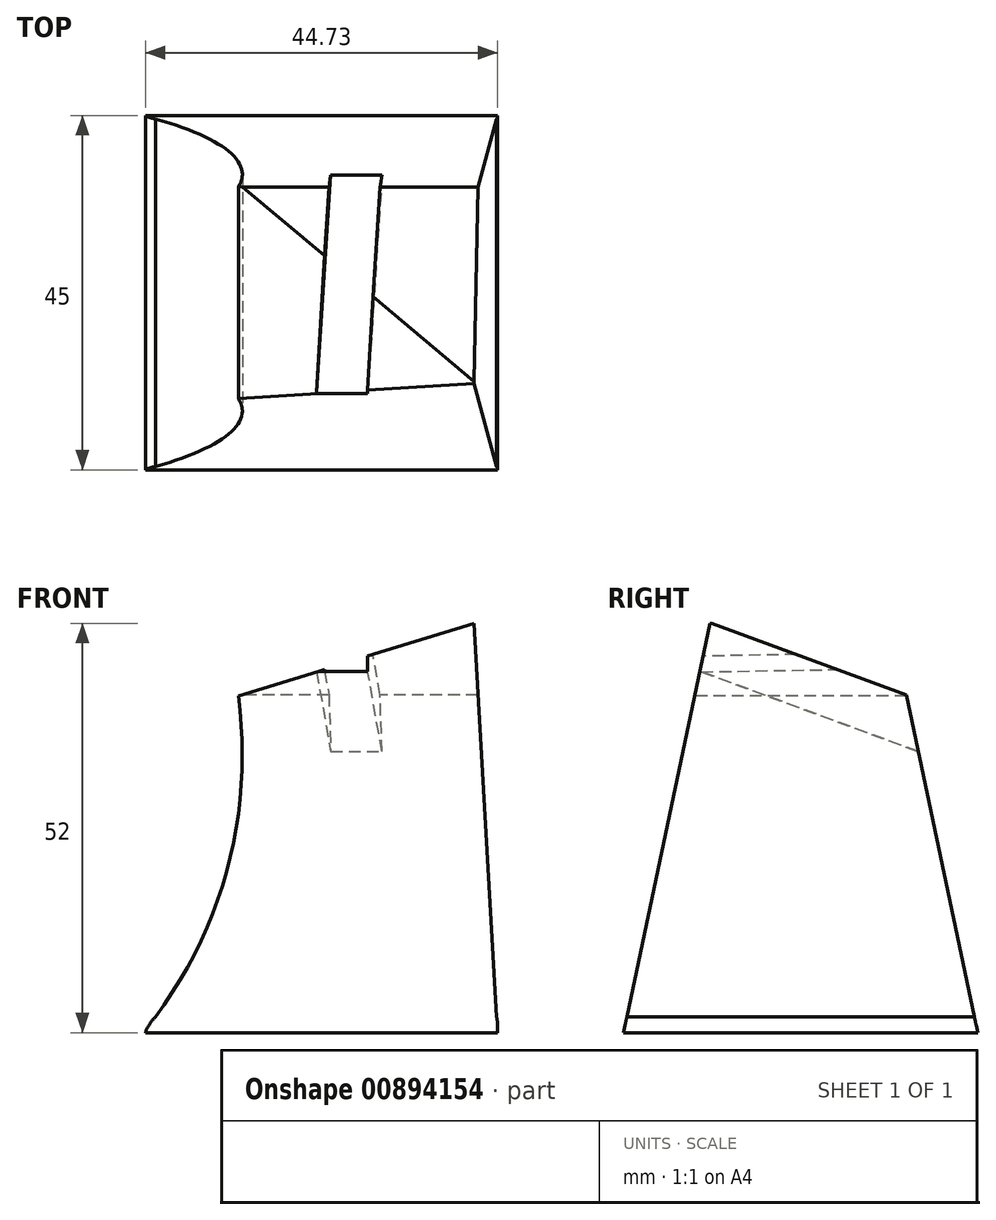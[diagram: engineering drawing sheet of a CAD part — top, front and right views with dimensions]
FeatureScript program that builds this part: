
annotation { "Feature Type Name" : "Feature", "Feature Type Description" : "" }
export const myFeature = defineFeature(function(context is Context, id is Id, definition is map)
    precondition{}
    {
        {
            var Q0;
            Q0=qCreatedBy(makeId("Top.planeOp"),FACE);
            var sketch = newSketch(context, id + "F0", { "sketchPlane" : qUnion([Q0])});
            skLineSegment(sketch, "E0", {"start": v(0, 45) * mm, "end": v(0, 0) * mm});
            skLineSegment(sketch, "E1.0", {"start": v(-45, 45) * mm, "end": v(-45, 0) * mm});
            skLineSegment(sketch, "E2", {"start": v(-45, 45) * mm, "end": v(0, 45) * mm});
            skLineSegment(sketch, "E3", {"start": v(-45, 0) * mm, "end": v(0, 0) * mm});
            skSolve(sketch);
        }
        {
            var Q0;
            Q0=makeQuery(id+"F0.imprint","IMPRINT",FACE,{"disambiguationData":[TD([[makeQuery(id+"F0.imprint","IMPRINT",EDGE,{"derivedFrom":sQuery(id+"F0.wireOp",EDGE,"E0")}),-1.0]])]});
            extrude(context, id + "F1", {"entities" : qUnion([Q0]), "depth" : 2 * mm, "offsetDistance" : 25 * mm});
        }
        {
            var Q0;
            Q0=qCreatedBy(makeId("Front.planeOp"),FACE);
            var sketch = newSketch(context, id + "F2", { "sketchPlane" : qUnion([Q0])});
            skLineSegment(sketch, "E4", {"start": v(0, 0) * mm, "end": v(-3, 52) * mm});
            skLineSegment(sketch, "E5", {"start": v(-3, 52) * mm, "end": v(-32.92, 42.77) * mm});
            skArc(sketch, "E6", {"start": v(-45, 0) * mm, "mid": v(-34.5, 20.13) * mm, "end": v(-32.92, 42.77) * mm});
            skLineSegment(sketch, "E7", {"start": v(-45, 0) * mm, "end": v(0, 0) * mm});
            skSolve(sketch);
        }
        {
            var Q0;
            Q0=makeQuery(id+"F2.imprint","IMPRINT",FACE,{"disambiguationData":[TD([[makeQuery(id+"F2.imprint","IMPRINT",EDGE,{"derivedFrom":sQuery(id+"F2.wireOp",EDGE,"E4")}),1.0]])]});
            extrude(context, id + "F3", {"entities" : qUnion([Q0]), "operationType" : NewBodyOperationType.ADD, "oppositeDirection" : true, "depth" : 45 * mm, "offsetDistance" : 25 * mm});
        }
        {
            var Q0;
            Q0=qCreatedBy(makeId("Right.planeOp"),FACE);
            var sketch = newSketch(context, id + "F4", { "sketchPlane" : qUnion([Q0])});
            skLineSegment(sketch, "E8", {"start": v(12.5, 59.13) * mm, "end": v(0, 0) * mm});
            skLineSegment(sketch, "E9", {"start": v(12.5, 59.13) * mm, "end": v(0, 59.13) * mm});
            skLineSegment(sketch, "E10", {"start": v(0, 59.13) * mm, "end": v(0, 0) * mm});
            skLineSegment(sketch, "E11.0", {"start": v(45, 59.13) * mm, "end": v(45, 0) * mm});
            skLineSegment(sketch, "E12", {"start": v(45, 0) * mm, "end": v(32.5, 59.13) * mm});
            skLineSegment(sketch, "E13", {"start": v(45, 59.13) * mm, "end": v(32.5, 59.13) * mm});
            skSolve(sketch);
        }
        {
            var Q0;
            Q0=makeQuery(id+"F4.imprint","IMPRINT",FACE,{"disambiguationData":[TD([[makeQuery(id+"F4.imprint","IMPRINT",EDGE,{"derivedFrom":sQuery(id+"F4.wireOp",EDGE,"E8")}),-1.0]])]});
            var Q1;
            Q1=makeQuery(id+"F4.imprint","IMPRINT",FACE,{"disambiguationData":[TD([[makeQuery(id+"F4.imprint","IMPRINT",EDGE,{"derivedFrom":sQuery(id+"F4.wireOp",EDGE,"E11.0")}),-1.0]])]});
            extrude(context, id + "F5", {"entities" : qUnion([Q0, Q1]), "operationType" : NewBodyOperationType.REMOVE, "oppositeDirection" : true, "depth" : 50 * mm, "offsetDistance" : 25 * mm});
        }
        {
            var Q0;
            Q0=qCreatedBy(makeId("Right.planeOp"),FACE);
            var sketch = newSketch(context, id + "F6", { "sketchPlane" : qUnion([Q0])});
            skLineSegment(sketch, "E14", {"start": v(10.98, 52.1) * mm, "end": v(37.77, 42.25) * mm});
            skLineSegment(sketch, "E15", {"start": v(37.77, 42.25) * mm, "end": v(37.77, 54.4) * mm});
            skLineSegment(sketch, "E16", {"start": v(37.77, 54.4) * mm, "end": v(10.98, 52.1) * mm});
            skSolve(sketch);
        }
        {
            var Q0;
            Q0=makeQuery(id+"F6.imprint","IMPRINT",FACE,{"disambiguationData":[TD([[makeQuery(id+"F6.imprint","IMPRINT",EDGE,{"derivedFrom":sQuery(id+"F6.wireOp",EDGE,"E14")}),1.0]])]});
            extrude(context, id + "F7", {"entities" : qUnion([Q0]), "operationType" : NewBodyOperationType.REMOVE, "oppositeDirection" : true, "depth" : 52.4 * mm, "offsetDistance" : 25 * mm});
        }
        {
            var Q0;
            Q0=makeQuery(id+"F7.boolean.opBoolean","COPY",FACE,{"derivedFrom":makeQuery(id+"F7.opExtrude","SWEPT_FACE",FACE,{"disambiguationData":[OSD([sQuery(id+"F6.wireOp",EDGE,"E14")])]})});
            var sketch = newSketch(context, id + "F8", { "sketchPlane" : qUnion([Q0])});
            skLineSegment(sketch, "E17", {"start": v(-13.47, 42.57) * mm, "end": v(-19.96, 42.96) * mm});
            skLineSegment(sketch, "E18.0", {"start": v(-23.57, -16.15) * mm, "end": v(-17.08, -16.54) * mm});
            skLineSegment(sketch, "E19", {"start": v(-13.47, 42.57) * mm, "end": v(-17.08, -16.54) * mm});
            skLineSegment(sketch, "E20", {"start": v(-23.57, -16.15) * mm, "end": v(-19.96, 42.96) * mm});
            skSolve(sketch);
        }
        {
            var Q0;
            {var subQ0=sQuery(id+"F8.wireOp",EDGE,"E17");Q0=makeQuery(id+"F8.imprint","IMPRINT",FACE,{"disambiguationData":[TD([[makeQuery(id+"F8.imprint","IMPRINT",EDGE,{"derivedFrom":subQ0}),1.0]])]});}
            var Q1;
            {var subQ0=sQuery(id+"F8.wireOp",EDGE,"E19");var subQ1=makeQuery(id+"F7.opExtrude","SWEPT_FACE",FACE,{"disambiguationData":[OSD([sQuery(id+"F6.wireOp",EDGE,"E14")])]});var subQ2=makeQuery(id+"F7.boolean.opBoolean","INTERSECT",EDGE,{"derivedFrom":[makeQuery(id+"F5.boolean.opBoolean","COPY",FACE,{"derivedFrom":makeQuery(id+"F5.opExtrude","SWEPT_FACE",FACE,{"disambiguationData":[OSD([sQuery(id+"F4.wireOp",EDGE,"E12")])]})}),subQ1]});var subQ3=makeQuery(id+"F8.imprint","INTERSECT",VERTEX,{"derivedFrom":[subQ2,subQ0]});Q1=makeQuery(id+"F8.imprint","IMPRINT",FACE,{"disambiguationData":[TD([[makeQuery(id+"F8.imprint","IMPRINT",EDGE,{"disambiguationData":[TD([[subQ3,-1.0]])],"derivedFrom":subQ0}),-1.0]])]});}
            var Q2;
            {var subQ0=sQuery(id+"F8.wireOp",EDGE,"E18.0");Q2=makeQuery(id+"F8.imprint","IMPRINT",FACE,{"disambiguationData":[TD([[makeQuery(id+"F8.imprint","IMPRINT",EDGE,{"derivedFrom":subQ0}),1.0]])]});}
            extrude(context, id + "F9", {"entities" : qUnion([Q0, Q1, Q2]), "operationType" : NewBodyOperationType.REMOVE, "oppositeDirection" : true, "depth" : 6.25 * mm, "offsetDistance" : 25 * mm});
        }
        {
            var Q0;
            Q0=makeQuery(id+"F1.opExtrude","CAP_EDGE",EDGE,{"disambiguationData":[OSD([sQuery(id+"F0.wireOp",EDGE,"E1.0")])],"isStart":false});
            fillet(context, id + "F10", {"entities" : qUnion([Q0]), "radius" : 5 * mm, "tangentPropagation" : true, "allowEdgeOverflow" : false});
        }
        {
            var Q0;
            Q0=makeQuery(id+"F1.opExtrude","CAP_EDGE",EDGE,{"disambiguationData":[OSD([sQuery(id+"F0.wireOp",EDGE,"E0")])],"isStart":false});
            fillet(context, id + "F11", {"entities" : qUnion([Q0]), "radius" : 5 * mm, "tangentPropagation" : true, "allowEdgeOverflow" : false});
        }
    });
